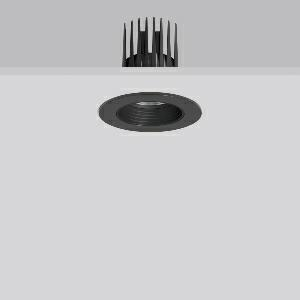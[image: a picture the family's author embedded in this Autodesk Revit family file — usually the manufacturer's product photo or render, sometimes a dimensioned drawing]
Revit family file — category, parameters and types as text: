
# Revit family: heledon_mini_e_901753_003_2_ea5f
name_source: partatom
category: Lighting Fixtures
units: mm (PartAtom-declared; Revit-internal decimal feet)

## family parameters
Cut with Voids When Loaded = No
Host = Face
Light Source = No
Part Type = Normal
Room Calculation Point = No
Round Connector Dimension = Use Diameter
Shared = No

## types (1)
- HELEDON mini E (1 x LED Modul 927, 2700 lm, 2700)
    Apparent Load = 29 VA
    Approval mark = CE
    CIE Flux Codes = 98 100 100 100 100
    Color Rendering = 92
    Color Temperature = 2700
    Default Elevation = 1800 mm
    Description = Series: HELEDON mini
Round recessed downlight. Housing: die-cast aluminium, powder-coated. Black plastic ring and recessed LED to prevent glare from the side. Optical assembly with lens made of plastic (polycarbonate) for the best homogeneous light distribution - can be changed without tools. Best colour rendering index Ra>90. Suitable for Recessed ceiling mounting. Installation without tools thanks to spring fastening system. Including separate LED converter with connecting cable 600 mm.High quality converter without flickering and stroboscopic effect. Through-wiring box (5 pole) available as accessory. The following accessories can be mounted without use of tools: interchangeable lenses, decorative glasses, honeycomb louvre, clear and frosted diffusers, white interchangeable plastic ring. 
Colour: deep black, matt (RAL 9005)
Diameter: 124 mm
Height: 3 mm
Cut-out diameter: 114 mm
Recess height: 170 mm
Luminaire: recess height: 120 mm
Lamp: LED
Socket: without socket
Colour temperature: 2700K
Colour rendering index (CRI): 92
System power: 29 W
Rated luminous flux: 2700 lm
Luminous efficiency: 93 lm/W
Control gear: Regulated power supply
Protection class: II
Type of protection: IP 20
    Height = 0 mm  [stored 0 ft]
    Lamp = 1 x LED Modul 927
    Lamp Light Flux = 2700 lm
    Lamp count = 1
    Length = 124 mm  [stored 0.406824 ft]
    Lifetime = 50000 h
    Luminous efficacy = 93 lm/W
    Manufacturer = RZB
    ModVariant = No
    Model = 901753.003.2
    Mounting Place = Ceiling
    Mounting Type = Recessed
    Number of Poles = 1
    OnlyDefault = Yes
    Power Factor = 1
    Product Name = HELEDON mini E
    Product group = Recessed downlights
    ProductGroupID = 402
    Protection Class = Protection class II
    Protection Degree = IP 20
    RLX_Detail_Level = 1
    RLX_Emergency_Light_Flux = 0 lm
    RLX_Emergency_Type = 0
    RLX_Emergency_Type_DB = No
    RlxData = <blob elided: 125601 chars, md5=ba6ac316>
    Socket = socket
    Standby Power = 0 W
    System Light Flux = 2700 lm
    System Power = 29 W
    Type Comments = Product without accessories
    Type Image = 901656.003.jpg
    URL = http://relux.com
    VarID = ---
    Voltage = 230 V
    Voltage Range = 220-240 V
    Weight = 0.00 kg
    Width = 0 mm  [stored 0 ft]

note: [stored X ft] marks values corroborated as IEEE doubles in the binary element streams (Revit-internal decimal feet)

## geometry (parser evidence)
native form markers: Blend x4, Sweep x11
no freeform markers — native parametric forms only
